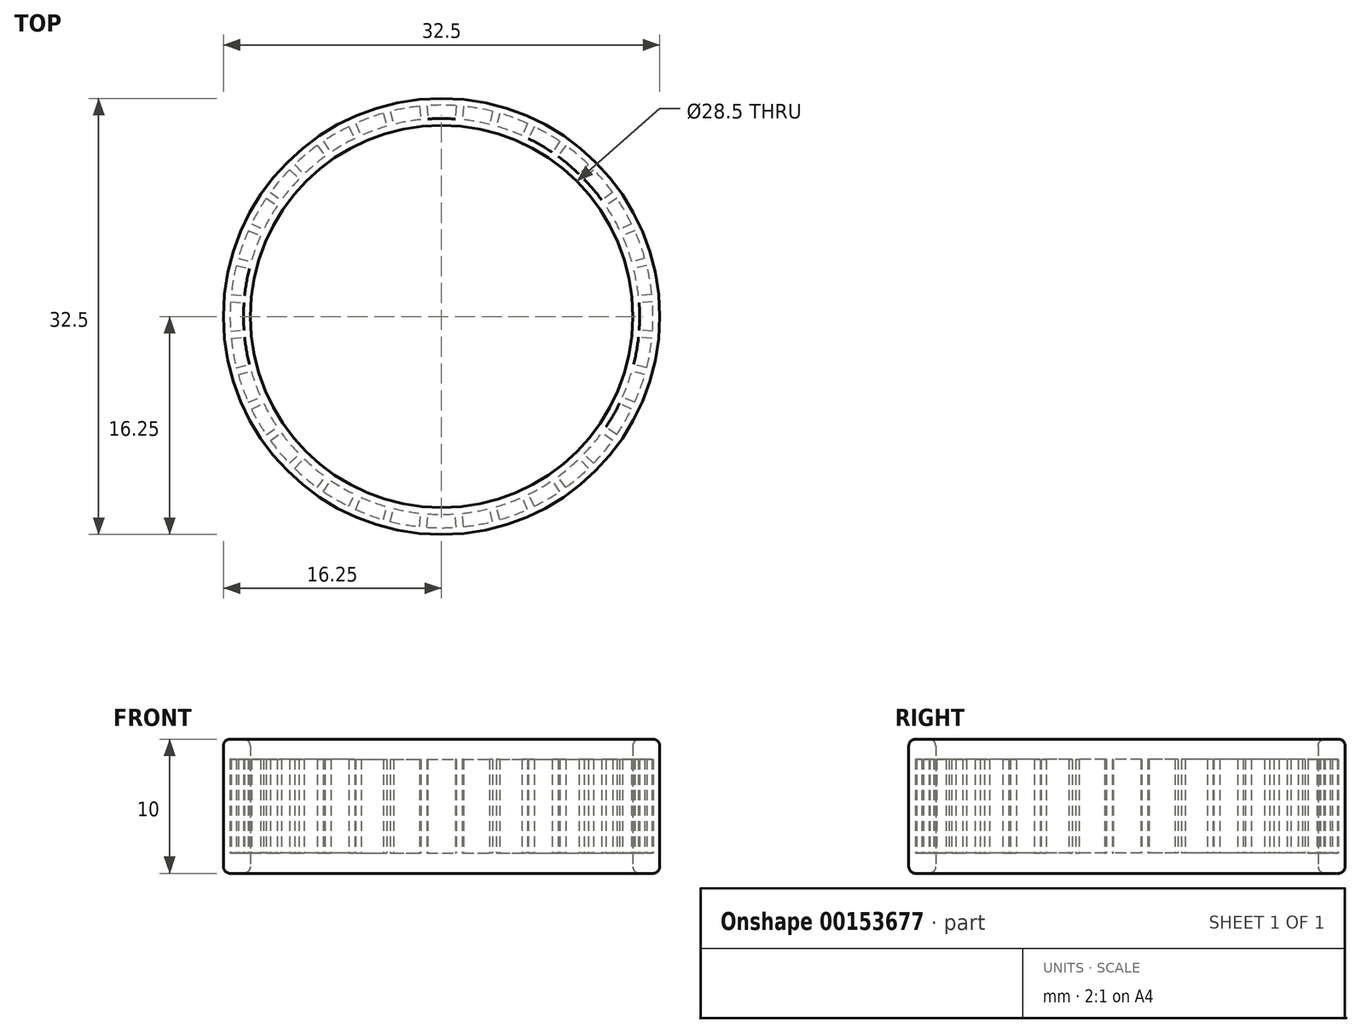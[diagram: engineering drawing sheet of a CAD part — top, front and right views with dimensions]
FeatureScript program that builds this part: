
annotation { "Feature Type Name" : "Feature", "Feature Type Description" : "" }
export const myFeature = defineFeature(function(context is Context, id is Id, definition is map)
    precondition{}
    {
        {
            var Q0;
            Q0=qCreatedBy(makeId("Top.planeOp"),FACE);
            var sketch = newSketch(context, id + "F0", { "sketchPlane" : qUnion([Q0])});
            skCircle(sketch, "E0", {"center": v(0, 0) * mm, "radius": 16.25 * mm});
            skCircle(sketch, "E1", {"center": v(0, 0) * mm, "radius": 14.25 * mm});
            skSolve(sketch);
        }
        {
            var Q0;
            Q0 = qSketchRegion(id + "F0", true);
            var Q1;
            Q1 = qConstructionFilter(qBodyType(qCreatedBy(id + "F0" ,EDGE), BodyType.WIRE), ConstructionObject.NO);
            extrude(context, id + "F1", {"entities" : qUnion([Q0]), "surfaceEntities" : qUnion([Q1]), "depth" : 1.5 * mm});
        }
        {
            var Q0;
            Q0=makeQuery(id+"F1.opExtrude","CAP_FACE",FACE,{"disambiguationData":[OSD([sQuery(id+"F0.wireOp",EDGE,"E0"),sQuery(id+"F0.wireOp",EDGE,"E1")])],"isStart":false});
            var sketch = newSketch(context, id + "F2", { "sketchPlane" : qUnion([Q0])});
            skCircle(sketch, "E2", {"center": v(0, 0) * mm, "radius": 16.25 * mm});
            skCircle(sketch, "E3", {"center": v(0, 0) * mm, "radius": 14.25 * mm});
            skArc(sketch, "E4", {"start": v(-1.03, 14.71) * mm, "mid": v(0, 14.75) * mm, "end": v(1.03, 14.71) * mm});
            skArc(sketch, "E5", {"start": v(-1.1, 15.71) * mm, "mid": v(0, 15.75) * mm, "end": v(1.1, 15.71) * mm});
            skLineSegment(sketch, "E6", {"start": v(-1.1, 15.71) * mm, "end": v(-1.03, 14.71) * mm});
            skLineSegment(sketch, "E7", {"start": v(1.1, 15.71) * mm, "end": v(1.03, 14.71) * mm});
            skLineSegment(sketch, "E8", {"start": v(0, 14.75) * mm, "end": v(0, 15.75) * mm, "construction": true});
            skLineSegment(sketch, "E9.1.0", {"start": v(-1.65, 15.66) * mm, "end": v(-1.54, 14.67) * mm});
            skArc(sketch, "E9.1.1", {"start": v(-3.81, 15.28) * mm, "mid": v(-2.73, 15.51) * mm, "end": v(-1.65, 15.66) * mm});
            skArc(sketch, "E9.1.2", {"start": v(-3.57, 14.31) * mm, "mid": v(-2.56, 14.53) * mm, "end": v(-1.54, 14.67) * mm});
            skLineSegment(sketch, "E9.1.3", {"start": v(-3.81, 15.28) * mm, "end": v(-3.57, 14.31) * mm});
            skLineSegment(sketch, "E9.2.0", {"start": v(-4.34, 15.14) * mm, "end": v(-4.07, 14.18) * mm});
            skArc(sketch, "E9.2.1", {"start": v(-6.4, 14.39) * mm, "mid": v(-5.39, 14.8) * mm, "end": v(-4.34, 15.14) * mm});
            skArc(sketch, "E9.2.2", {"start": v(-6, 13.47) * mm, "mid": v(-5.04, 13.86) * mm, "end": v(-4.07, 14.18) * mm});
            skLineSegment(sketch, "E9.2.3", {"start": v(-6.4, 14.39) * mm, "end": v(-6, 13.47) * mm});
            skLineSegment(sketch, "E9.3.0", {"start": v(-6.9, 14.16) * mm, "end": v(-6.47, 13.26) * mm});
            skArc(sketch, "E9.3.1", {"start": v(-8.8, 13.06) * mm, "mid": v(-7.87, 13.64) * mm, "end": v(-6.9, 14.16) * mm});
            skArc(sketch, "E9.3.2", {"start": v(-8.25, 12.23) * mm, "mid": v(-7.38, 12.77) * mm, "end": v(-6.47, 13.26) * mm});
            skLineSegment(sketch, "E9.3.3", {"start": v(-8.8, 13.06) * mm, "end": v(-8.25, 12.23) * mm});
            skLineSegment(sketch, "E9.4.0", {"start": v(-9.26, 12.74) * mm, "end": v(-8.67, 11.93) * mm});
            skArc(sketch, "E9.4.1", {"start": v(-10.94, 11.33) * mm, "mid": v(-10.12, 12.07) * mm, "end": v(-9.26, 12.74) * mm});
            skArc(sketch, "E9.4.2", {"start": v(-10.25, 10.61) * mm, "mid": v(-9.48, 11.3) * mm, "end": v(-8.67, 11.93) * mm});
            skLineSegment(sketch, "E9.4.3", {"start": v(-10.94, 11.33) * mm, "end": v(-10.25, 10.61) * mm});
            skLineSegment(sketch, "E9.5.0", {"start": v(-11.33, 10.94) * mm, "end": v(-10.61, 10.25) * mm});
            skArc(sketch, "E9.5.1", {"start": v(-12.74, 9.26) * mm, "mid": v(-12.07, 10.12) * mm, "end": v(-11.33, 10.94) * mm});
            skArc(sketch, "E9.5.2", {"start": v(-11.93, 8.67) * mm, "mid": v(-11.3, 9.48) * mm, "end": v(-10.61, 10.25) * mm});
            skLineSegment(sketch, "E9.5.3", {"start": v(-12.74, 9.26) * mm, "end": v(-11.93, 8.67) * mm});
            skLineSegment(sketch, "E9.6.0", {"start": v(-13.06, 8.8) * mm, "end": v(-12.23, 8.25) * mm});
            skArc(sketch, "E9.6.1", {"start": v(-14.16, 6.9) * mm, "mid": v(-13.64, 7.88) * mm, "end": v(-13.06, 8.8) * mm});
            skArc(sketch, "E9.6.2", {"start": v(-13.26, 6.47) * mm, "mid": v(-12.77, 7.38) * mm, "end": v(-12.23, 8.25) * mm});
            skLineSegment(sketch, "E9.6.3", {"start": v(-14.16, 6.9) * mm, "end": v(-13.26, 6.47) * mm});
            skLineSegment(sketch, "E9.7.0", {"start": v(-14.39, 6.4) * mm, "end": v(-13.47, 6) * mm});
            skArc(sketch, "E9.7.1", {"start": v(-15.14, 4.34) * mm, "mid": v(-14.8, 5.39) * mm, "end": v(-14.39, 6.4) * mm});
            skArc(sketch, "E9.7.2", {"start": v(-14.18, 4.07) * mm, "mid": v(-13.86, 5.04) * mm, "end": v(-13.47, 6) * mm});
            skLineSegment(sketch, "E9.7.3", {"start": v(-15.14, 4.34) * mm, "end": v(-14.18, 4.07) * mm});
            skLineSegment(sketch, "E9.8.0", {"start": v(-15.28, 3.81) * mm, "end": v(-14.31, 3.57) * mm});
            skArc(sketch, "E9.8.1", {"start": v(-15.66, 1.65) * mm, "mid": v(-15.51, 2.73) * mm, "end": v(-15.28, 3.81) * mm});
            skArc(sketch, "E9.8.2", {"start": v(-14.67, 1.54) * mm, "mid": v(-14.53, 2.56) * mm, "end": v(-14.31, 3.57) * mm});
            skLineSegment(sketch, "E9.8.3", {"start": v(-15.66, 1.65) * mm, "end": v(-14.67, 1.54) * mm});
            skLineSegment(sketch, "E9.9.0", {"start": v(-15.71, 1.1) * mm, "end": v(-14.71, 1.03) * mm});
            skArc(sketch, "E9.9.1", {"start": v(-15.71, -1.1) * mm, "mid": v(-15.75, 0) * mm, "end": v(-15.71, 1.1) * mm});
            skArc(sketch, "E9.9.2", {"start": v(-14.71, -1.03) * mm, "mid": v(-14.75, 0) * mm, "end": v(-14.71, 1.03) * mm});
            skLineSegment(sketch, "E9.9.3", {"start": v(-15.71, -1.1) * mm, "end": v(-14.71, -1.03) * mm});
            skLineSegment(sketch, "E9.10.0", {"start": v(-15.66, -1.65) * mm, "end": v(-14.67, -1.54) * mm});
            skArc(sketch, "E9.10.1", {"start": v(-15.28, -3.81) * mm, "mid": v(-15.51, -2.73) * mm, "end": v(-15.66, -1.65) * mm});
            skArc(sketch, "E9.10.2", {"start": v(-14.31, -3.57) * mm, "mid": v(-14.53, -2.56) * mm, "end": v(-14.67, -1.54) * mm});
            skLineSegment(sketch, "E9.10.3", {"start": v(-15.28, -3.81) * mm, "end": v(-14.31, -3.57) * mm});
            skLineSegment(sketch, "E9.11.0", {"start": v(-15.14, -4.34) * mm, "end": v(-14.18, -4.07) * mm});
            skArc(sketch, "E9.11.1", {"start": v(-14.39, -6.4) * mm, "mid": v(-14.8, -5.39) * mm, "end": v(-15.14, -4.34) * mm});
            skArc(sketch, "E9.11.2", {"start": v(-13.47, -6) * mm, "mid": v(-13.86, -5.04) * mm, "end": v(-14.18, -4.07) * mm});
            skLineSegment(sketch, "E9.11.3", {"start": v(-14.39, -6.4) * mm, "end": v(-13.47, -6) * mm});
            skLineSegment(sketch, "E9.12.0", {"start": v(-14.16, -6.9) * mm, "end": v(-13.26, -6.47) * mm});
            skArc(sketch, "E9.12.1", {"start": v(-13.06, -8.8) * mm, "mid": v(-13.64, -7.87) * mm, "end": v(-14.16, -6.9) * mm});
            skArc(sketch, "E9.12.2", {"start": v(-12.23, -8.25) * mm, "mid": v(-12.77, -7.37) * mm, "end": v(-13.26, -6.47) * mm});
            skLineSegment(sketch, "E9.12.3", {"start": v(-13.06, -8.8) * mm, "end": v(-12.23, -8.25) * mm});
            skLineSegment(sketch, "E9.13.0", {"start": v(-12.74, -9.26) * mm, "end": v(-11.93, -8.67) * mm});
            skArc(sketch, "E9.13.1", {"start": v(-11.33, -10.94) * mm, "mid": v(-12.07, -10.12) * mm, "end": v(-12.74, -9.26) * mm});
            skArc(sketch, "E9.13.2", {"start": v(-10.61, -10.25) * mm, "mid": v(-11.3, -9.48) * mm, "end": v(-11.93, -8.67) * mm});
            skLineSegment(sketch, "E9.13.3", {"start": v(-11.33, -10.94) * mm, "end": v(-10.61, -10.25) * mm});
            skLineSegment(sketch, "E9.14.0", {"start": v(-10.94, -11.33) * mm, "end": v(-10.25, -10.61) * mm});
            skArc(sketch, "E9.14.1", {"start": v(-9.26, -12.74) * mm, "mid": v(-10.12, -12.07) * mm, "end": v(-10.94, -11.33) * mm});
            skArc(sketch, "E9.14.2", {"start": v(-8.67, -11.93) * mm, "mid": v(-9.48, -11.3) * mm, "end": v(-10.25, -10.61) * mm});
            skLineSegment(sketch, "E9.14.3", {"start": v(-9.26, -12.74) * mm, "end": v(-8.67, -11.93) * mm});
            skLineSegment(sketch, "E9.15.0", {"start": v(-8.8, -13.06) * mm, "end": v(-8.25, -12.23) * mm});
            skArc(sketch, "E9.15.1", {"start": v(-6.9, -14.16) * mm, "mid": v(-7.87, -13.64) * mm, "end": v(-8.8, -13.06) * mm});
            skArc(sketch, "E9.15.2", {"start": v(-6.47, -13.26) * mm, "mid": v(-7.37, -12.77) * mm, "end": v(-8.25, -12.23) * mm});
            skLineSegment(sketch, "E9.15.3", {"start": v(-6.9, -14.16) * mm, "end": v(-6.47, -13.26) * mm});
            skLineSegment(sketch, "E9.16.0", {"start": v(-6.4, -14.39) * mm, "end": v(-6, -13.47) * mm});
            skArc(sketch, "E9.16.1", {"start": v(-4.34, -15.14) * mm, "mid": v(-5.39, -14.8) * mm, "end": v(-6.4, -14.39) * mm});
            skArc(sketch, "E9.16.2", {"start": v(-4.07, -14.18) * mm, "mid": v(-5.04, -13.86) * mm, "end": v(-6, -13.47) * mm});
            skLineSegment(sketch, "E9.16.3", {"start": v(-4.34, -15.14) * mm, "end": v(-4.07, -14.18) * mm});
            skLineSegment(sketch, "E9.17.0", {"start": v(-3.81, -15.28) * mm, "end": v(-3.57, -14.31) * mm});
            skArc(sketch, "E9.17.1", {"start": v(-1.65, -15.66) * mm, "mid": v(-2.73, -15.51) * mm, "end": v(-3.81, -15.28) * mm});
            skArc(sketch, "E9.17.2", {"start": v(-1.54, -14.67) * mm, "mid": v(-2.56, -14.53) * mm, "end": v(-3.57, -14.31) * mm});
            skLineSegment(sketch, "E9.17.3", {"start": v(-1.65, -15.66) * mm, "end": v(-1.54, -14.67) * mm});
            skLineSegment(sketch, "E9.18.0", {"start": v(-1.1, -15.71) * mm, "end": v(-1.03, -14.71) * mm});
            skArc(sketch, "E9.18.1", {"start": v(1.1, -15.71) * mm, "mid": v(0, -15.75) * mm, "end": v(-1.1, -15.71) * mm});
            skArc(sketch, "E9.18.2", {"start": v(1.03, -14.71) * mm, "mid": v(0, -14.75) * mm, "end": v(-1.03, -14.71) * mm});
            skLineSegment(sketch, "E9.18.3", {"start": v(1.1, -15.71) * mm, "end": v(1.03, -14.71) * mm});
            skLineSegment(sketch, "E9.19.0", {"start": v(1.65, -15.66) * mm, "end": v(1.54, -14.67) * mm});
            skArc(sketch, "E9.19.1", {"start": v(3.81, -15.28) * mm, "mid": v(2.73, -15.51) * mm, "end": v(1.65, -15.66) * mm});
            skArc(sketch, "E9.19.2", {"start": v(3.57, -14.31) * mm, "mid": v(2.56, -14.53) * mm, "end": v(1.54, -14.67) * mm});
            skLineSegment(sketch, "E9.19.3", {"start": v(3.81, -15.28) * mm, "end": v(3.57, -14.31) * mm});
            skLineSegment(sketch, "E9.20.0", {"start": v(4.34, -15.14) * mm, "end": v(4.07, -14.18) * mm});
            skArc(sketch, "E9.20.1", {"start": v(6.4, -14.39) * mm, "mid": v(5.39, -14.8) * mm, "end": v(4.34, -15.14) * mm});
            skArc(sketch, "E9.20.2", {"start": v(6, -13.47) * mm, "mid": v(5.04, -13.86) * mm, "end": v(4.07, -14.18) * mm});
            skLineSegment(sketch, "E9.20.3", {"start": v(6.4, -14.39) * mm, "end": v(6, -13.47) * mm});
            skLineSegment(sketch, "E9.21.0", {"start": v(6.9, -14.16) * mm, "end": v(6.47, -13.26) * mm});
            skArc(sketch, "E9.21.1", {"start": v(8.8, -13.06) * mm, "mid": v(7.87, -13.64) * mm, "end": v(6.9, -14.16) * mm});
            skArc(sketch, "E9.21.2", {"start": v(8.25, -12.23) * mm, "mid": v(7.37, -12.77) * mm, "end": v(6.47, -13.26) * mm});
            skLineSegment(sketch, "E9.21.3", {"start": v(8.8, -13.06) * mm, "end": v(8.25, -12.23) * mm});
            skLineSegment(sketch, "E9.22.0", {"start": v(9.26, -12.74) * mm, "end": v(8.67, -11.93) * mm});
            skArc(sketch, "E9.22.1", {"start": v(10.94, -11.33) * mm, "mid": v(10.12, -12.07) * mm, "end": v(9.26, -12.74) * mm});
            skArc(sketch, "E9.22.2", {"start": v(10.25, -10.61) * mm, "mid": v(9.48, -11.3) * mm, "end": v(8.67, -11.93) * mm});
            skLineSegment(sketch, "E9.22.3", {"start": v(10.94, -11.33) * mm, "end": v(10.25, -10.61) * mm});
            skLineSegment(sketch, "E9.23.0", {"start": v(11.33, -10.94) * mm, "end": v(10.61, -10.25) * mm});
            skArc(sketch, "E9.23.1", {"start": v(12.74, -9.26) * mm, "mid": v(12.07, -10.12) * mm, "end": v(11.33, -10.94) * mm});
            skArc(sketch, "E9.23.2", {"start": v(11.93, -8.67) * mm, "mid": v(11.3, -9.48) * mm, "end": v(10.61, -10.25) * mm});
            skLineSegment(sketch, "E9.23.3", {"start": v(12.74, -9.26) * mm, "end": v(11.93, -8.67) * mm});
            skLineSegment(sketch, "E9.24.0", {"start": v(13.06, -8.8) * mm, "end": v(12.23, -8.25) * mm});
            skArc(sketch, "E9.24.1", {"start": v(14.16, -6.9) * mm, "mid": v(13.64, -7.88) * mm, "end": v(13.06, -8.8) * mm});
            skArc(sketch, "E9.24.2", {"start": v(13.26, -6.47) * mm, "mid": v(12.77, -7.38) * mm, "end": v(12.23, -8.25) * mm});
            skLineSegment(sketch, "E9.24.3", {"start": v(14.16, -6.9) * mm, "end": v(13.26, -6.47) * mm});
            skLineSegment(sketch, "E9.25.0", {"start": v(14.39, -6.4) * mm, "end": v(13.47, -6) * mm});
            skArc(sketch, "E9.25.1", {"start": v(15.14, -4.34) * mm, "mid": v(14.8, -5.39) * mm, "end": v(14.39, -6.4) * mm});
            skArc(sketch, "E9.25.2", {"start": v(14.18, -4.07) * mm, "mid": v(13.86, -5.04) * mm, "end": v(13.47, -6) * mm});
            skLineSegment(sketch, "E9.25.3", {"start": v(15.14, -4.34) * mm, "end": v(14.18, -4.07) * mm});
            skLineSegment(sketch, "E9.26.0", {"start": v(15.28, -3.81) * mm, "end": v(14.31, -3.57) * mm});
            skArc(sketch, "E9.26.1", {"start": v(15.66, -1.65) * mm, "mid": v(15.51, -2.73) * mm, "end": v(15.28, -3.81) * mm});
            skArc(sketch, "E9.26.2", {"start": v(14.67, -1.54) * mm, "mid": v(14.53, -2.56) * mm, "end": v(14.31, -3.57) * mm});
            skLineSegment(sketch, "E9.26.3", {"start": v(15.66, -1.65) * mm, "end": v(14.67, -1.54) * mm});
            skLineSegment(sketch, "E9.27.0", {"start": v(15.71, -1.1) * mm, "end": v(14.71, -1.03) * mm});
            skArc(sketch, "E9.27.1", {"start": v(15.71, 1.1) * mm, "mid": v(15.75, 0) * mm, "end": v(15.71, -1.1) * mm});
            skArc(sketch, "E9.27.2", {"start": v(14.71, 1.03) * mm, "mid": v(14.75, 0) * mm, "end": v(14.71, -1.03) * mm});
            skLineSegment(sketch, "E9.27.3", {"start": v(15.71, 1.1) * mm, "end": v(14.71, 1.03) * mm});
            skLineSegment(sketch, "E9.28.0", {"start": v(15.66, 1.65) * mm, "end": v(14.67, 1.54) * mm});
            skArc(sketch, "E9.28.1", {"start": v(15.28, 3.81) * mm, "mid": v(15.51, 2.73) * mm, "end": v(15.66, 1.65) * mm});
            skArc(sketch, "E9.28.2", {"start": v(14.31, 3.57) * mm, "mid": v(14.53, 2.56) * mm, "end": v(14.67, 1.54) * mm});
            skLineSegment(sketch, "E9.28.3", {"start": v(15.28, 3.81) * mm, "end": v(14.31, 3.57) * mm});
            skLineSegment(sketch, "E9.29.0", {"start": v(15.14, 4.34) * mm, "end": v(14.18, 4.07) * mm});
            skArc(sketch, "E9.29.1", {"start": v(14.39, 6.4) * mm, "mid": v(14.8, 5.39) * mm, "end": v(15.14, 4.34) * mm});
            skArc(sketch, "E9.29.2", {"start": v(13.47, 6) * mm, "mid": v(13.86, 5.04) * mm, "end": v(14.18, 4.07) * mm});
            skLineSegment(sketch, "E9.29.3", {"start": v(14.39, 6.4) * mm, "end": v(13.47, 6) * mm});
            skLineSegment(sketch, "E9.30.0", {"start": v(14.16, 6.9) * mm, "end": v(13.26, 6.47) * mm});
            skArc(sketch, "E9.30.1", {"start": v(13.06, 8.8) * mm, "mid": v(13.64, 7.88) * mm, "end": v(14.16, 6.9) * mm});
            skArc(sketch, "E9.30.2", {"start": v(12.23, 8.25) * mm, "mid": v(12.77, 7.38) * mm, "end": v(13.26, 6.47) * mm});
            skLineSegment(sketch, "E9.30.3", {"start": v(13.06, 8.8) * mm, "end": v(12.23, 8.25) * mm});
            skLineSegment(sketch, "E9.31.0", {"start": v(12.74, 9.26) * mm, "end": v(11.93, 8.67) * mm});
            skArc(sketch, "E9.31.1", {"start": v(11.33, 10.94) * mm, "mid": v(12.07, 10.12) * mm, "end": v(12.74, 9.26) * mm});
            skArc(sketch, "E9.31.2", {"start": v(10.61, 10.25) * mm, "mid": v(11.3, 9.48) * mm, "end": v(11.93, 8.67) * mm});
            skLineSegment(sketch, "E9.31.3", {"start": v(11.33, 10.94) * mm, "end": v(10.61, 10.25) * mm});
            skLineSegment(sketch, "E9.32.0", {"start": v(10.94, 11.33) * mm, "end": v(10.25, 10.61) * mm});
            skArc(sketch, "E9.32.1", {"start": v(9.26, 12.74) * mm, "mid": v(10.12, 12.07) * mm, "end": v(10.94, 11.33) * mm});
            skArc(sketch, "E9.32.2", {"start": v(8.67, 11.93) * mm, "mid": v(9.48, 11.3) * mm, "end": v(10.25, 10.61) * mm});
            skLineSegment(sketch, "E9.32.3", {"start": v(9.26, 12.74) * mm, "end": v(8.67, 11.93) * mm});
            skLineSegment(sketch, "E9.33.0", {"start": v(8.8, 13.06) * mm, "end": v(8.25, 12.23) * mm});
            skArc(sketch, "E9.33.1", {"start": v(6.9, 14.16) * mm, "mid": v(7.88, 13.64) * mm, "end": v(8.8, 13.06) * mm});
            skArc(sketch, "E9.33.2", {"start": v(6.47, 13.26) * mm, "mid": v(7.38, 12.77) * mm, "end": v(8.25, 12.23) * mm});
            skLineSegment(sketch, "E9.33.3", {"start": v(6.9, 14.16) * mm, "end": v(6.47, 13.26) * mm});
            skLineSegment(sketch, "E9.34.0", {"start": v(6.4, 14.39) * mm, "end": v(6, 13.47) * mm});
            skArc(sketch, "E9.34.1", {"start": v(4.34, 15.14) * mm, "mid": v(5.39, 14.8) * mm, "end": v(6.4, 14.39) * mm});
            skArc(sketch, "E9.34.2", {"start": v(4.07, 14.18) * mm, "mid": v(5.04, 13.86) * mm, "end": v(6, 13.47) * mm});
            skLineSegment(sketch, "E9.34.3", {"start": v(4.34, 15.14) * mm, "end": v(4.07, 14.18) * mm});
            skLineSegment(sketch, "E9.35.0", {"start": v(3.81, 15.28) * mm, "end": v(3.57, 14.31) * mm});
            skArc(sketch, "E9.35.1", {"start": v(1.65, 15.66) * mm, "mid": v(2.73, 15.51) * mm, "end": v(3.81, 15.28) * mm});
            skArc(sketch, "E9.35.2", {"start": v(1.54, 14.67) * mm, "mid": v(2.56, 14.53) * mm, "end": v(3.57, 14.31) * mm});
            skLineSegment(sketch, "E9.35.3", {"start": v(1.65, 15.66) * mm, "end": v(1.54, 14.67) * mm});
            skSolve(sketch);
        }
        {
            var Q0;
            Q0 = qSketchRegion(id + "F2", true);
            extrude(context, id + "F3", {"entities" : qUnion([Q0]), "operationType" : NewBodyOperationType.ADD, "depth" : 7 * mm});
        }
        {
            var Q0;
            Q0=makeQuery(id+"F3.opExtrude","CAP_FACE",FACE,{"disambiguationData":[OSD([sQuery(id+"F2.wireOp",EDGE,"E2"),sQuery(id+"F2.wireOp",EDGE,"E3"),sQuery(id+"F2.wireOp",EDGE,"E4"),sQuery(id+"F2.wireOp",EDGE,"E5"),sQuery(id+"F2.wireOp",EDGE,"E6"),sQuery(id+"F2.wireOp",EDGE,"E7"),sQuery(id+"F2.wireOp",EDGE,"E9.1.0"),sQuery(id+"F2.wireOp",EDGE,"E9.1.1"),sQuery(id+"F2.wireOp",EDGE,"E9.1.2"),sQuery(id+"F2.wireOp",EDGE,"E9.1.3"),sQuery(id+"F2.wireOp",EDGE,"E9.2.0"),sQuery(id+"F2.wireOp",EDGE,"E9.2.1"),sQuery(id+"F2.wireOp",EDGE,"E9.2.2"),sQuery(id+"F2.wireOp",EDGE,"E9.2.3"),sQuery(id+"F2.wireOp",EDGE,"E9.3.0"),sQuery(id+"F2.wireOp",EDGE,"E9.3.1"),sQuery(id+"F2.wireOp",EDGE,"E9.3.2"),sQuery(id+"F2.wireOp",EDGE,"E9.3.3"),sQuery(id+"F2.wireOp",EDGE,"E9.4.0"),sQuery(id+"F2.wireOp",EDGE,"E9.4.1"),sQuery(id+"F2.wireOp",EDGE,"E9.4.2"),sQuery(id+"F2.wireOp",EDGE,"E9.4.3"),sQuery(id+"F2.wireOp",EDGE,"E9.5.0"),sQuery(id+"F2.wireOp",EDGE,"E9.5.1"),sQuery(id+"F2.wireOp",EDGE,"E9.5.2"),sQuery(id+"F2.wireOp",EDGE,"E9.5.3"),sQuery(id+"F2.wireOp",EDGE,"E9.6.0"),sQuery(id+"F2.wireOp",EDGE,"E9.6.1"),sQuery(id+"F2.wireOp",EDGE,"E9.6.2"),sQuery(id+"F2.wireOp",EDGE,"E9.6.3"),sQuery(id+"F2.wireOp",EDGE,"E9.7.0"),sQuery(id+"F2.wireOp",EDGE,"E9.7.1"),sQuery(id+"F2.wireOp",EDGE,"E9.7.2"),sQuery(id+"F2.wireOp",EDGE,"E9.7.3"),sQuery(id+"F2.wireOp",EDGE,"E9.8.0"),sQuery(id+"F2.wireOp",EDGE,"E9.8.1"),sQuery(id+"F2.wireOp",EDGE,"E9.8.2"),sQuery(id+"F2.wireOp",EDGE,"E9.8.3"),sQuery(id+"F2.wireOp",EDGE,"E9.9.0"),sQuery(id+"F2.wireOp",EDGE,"E9.9.1"),sQuery(id+"F2.wireOp",EDGE,"E9.9.2"),sQuery(id+"F2.wireOp",EDGE,"E9.9.3"),sQuery(id+"F2.wireOp",EDGE,"E9.10.0"),sQuery(id+"F2.wireOp",EDGE,"E9.10.1"),sQuery(id+"F2.wireOp",EDGE,"E9.10.2"),sQuery(id+"F2.wireOp",EDGE,"E9.10.3"),sQuery(id+"F2.wireOp",EDGE,"E9.11.0"),sQuery(id+"F2.wireOp",EDGE,"E9.11.1"),sQuery(id+"F2.wireOp",EDGE,"E9.11.2"),sQuery(id+"F2.wireOp",EDGE,"E9.11.3"),sQuery(id+"F2.wireOp",EDGE,"E9.12.0"),sQuery(id+"F2.wireOp",EDGE,"E9.12.1"),sQuery(id+"F2.wireOp",EDGE,"E9.12.2"),sQuery(id+"F2.wireOp",EDGE,"E9.12.3"),sQuery(id+"F2.wireOp",EDGE,"E9.13.0"),sQuery(id+"F2.wireOp",EDGE,"E9.13.1"),sQuery(id+"F2.wireOp",EDGE,"E9.13.2"),sQuery(id+"F2.wireOp",EDGE,"E9.13.3"),sQuery(id+"F2.wireOp",EDGE,"E9.14.0"),sQuery(id+"F2.wireOp",EDGE,"E9.14.1"),sQuery(id+"F2.wireOp",EDGE,"E9.14.2"),sQuery(id+"F2.wireOp",EDGE,"E9.14.3"),sQuery(id+"F2.wireOp",EDGE,"E9.15.0"),sQuery(id+"F2.wireOp",EDGE,"E9.15.1"),sQuery(id+"F2.wireOp",EDGE,"E9.15.2"),sQuery(id+"F2.wireOp",EDGE,"E9.15.3"),sQuery(id+"F2.wireOp",EDGE,"E9.16.0"),sQuery(id+"F2.wireOp",EDGE,"E9.16.1"),sQuery(id+"F2.wireOp",EDGE,"E9.16.2"),sQuery(id+"F2.wireOp",EDGE,"E9.16.3"),sQuery(id+"F2.wireOp",EDGE,"E9.17.0"),sQuery(id+"F2.wireOp",EDGE,"E9.17.1"),sQuery(id+"F2.wireOp",EDGE,"E9.17.2"),sQuery(id+"F2.wireOp",EDGE,"E9.17.3"),sQuery(id+"F2.wireOp",EDGE,"E9.18.0"),sQuery(id+"F2.wireOp",EDGE,"E9.18.1"),sQuery(id+"F2.wireOp",EDGE,"E9.18.2"),sQuery(id+"F2.wireOp",EDGE,"E9.18.3"),sQuery(id+"F2.wireOp",EDGE,"E9.19.0"),sQuery(id+"F2.wireOp",EDGE,"E9.19.1"),sQuery(id+"F2.wireOp",EDGE,"E9.19.2"),sQuery(id+"F2.wireOp",EDGE,"E9.19.3"),sQuery(id+"F2.wireOp",EDGE,"E9.20.0"),sQuery(id+"F2.wireOp",EDGE,"E9.20.1"),sQuery(id+"F2.wireOp",EDGE,"E9.20.2"),sQuery(id+"F2.wireOp",EDGE,"E9.20.3"),sQuery(id+"F2.wireOp",EDGE,"E9.21.0"),sQuery(id+"F2.wireOp",EDGE,"E9.21.1"),sQuery(id+"F2.wireOp",EDGE,"E9.21.2"),sQuery(id+"F2.wireOp",EDGE,"E9.21.3"),sQuery(id+"F2.wireOp",EDGE,"E9.22.0"),sQuery(id+"F2.wireOp",EDGE,"E9.22.1"),sQuery(id+"F2.wireOp",EDGE,"E9.22.2"),sQuery(id+"F2.wireOp",EDGE,"E9.22.3"),sQuery(id+"F2.wireOp",EDGE,"E9.23.0"),sQuery(id+"F2.wireOp",EDGE,"E9.23.1"),sQuery(id+"F2.wireOp",EDGE,"E9.23.2"),sQuery(id+"F2.wireOp",EDGE,"E9.23.3"),sQuery(id+"F2.wireOp",EDGE,"E9.24.0"),sQuery(id+"F2.wireOp",EDGE,"E9.24.1"),sQuery(id+"F2.wireOp",EDGE,"E9.24.2"),sQuery(id+"F2.wireOp",EDGE,"E9.24.3"),sQuery(id+"F2.wireOp",EDGE,"E9.25.0"),sQuery(id+"F2.wireOp",EDGE,"E9.25.1"),sQuery(id+"F2.wireOp",EDGE,"E9.25.2"),sQuery(id+"F2.wireOp",EDGE,"E9.25.3"),sQuery(id+"F2.wireOp",EDGE,"E9.26.0"),sQuery(id+"F2.wireOp",EDGE,"E9.26.1"),sQuery(id+"F2.wireOp",EDGE,"E9.26.2"),sQuery(id+"F2.wireOp",EDGE,"E9.26.3"),sQuery(id+"F2.wireOp",EDGE,"E9.27.0"),sQuery(id+"F2.wireOp",EDGE,"E9.27.1"),sQuery(id+"F2.wireOp",EDGE,"E9.27.2"),sQuery(id+"F2.wireOp",EDGE,"E9.27.3"),sQuery(id+"F2.wireOp",EDGE,"E9.28.0"),sQuery(id+"F2.wireOp",EDGE,"E9.28.1"),sQuery(id+"F2.wireOp",EDGE,"E9.28.2"),sQuery(id+"F2.wireOp",EDGE,"E9.28.3"),sQuery(id+"F2.wireOp",EDGE,"E9.29.0"),sQuery(id+"F2.wireOp",EDGE,"E9.29.1"),sQuery(id+"F2.wireOp",EDGE,"E9.29.2"),sQuery(id+"F2.wireOp",EDGE,"E9.29.3"),sQuery(id+"F2.wireOp",EDGE,"E9.30.0"),sQuery(id+"F2.wireOp",EDGE,"E9.30.1"),sQuery(id+"F2.wireOp",EDGE,"E9.30.2"),sQuery(id+"F2.wireOp",EDGE,"E9.30.3"),sQuery(id+"F2.wireOp",EDGE,"E9.31.0"),sQuery(id+"F2.wireOp",EDGE,"E9.31.1"),sQuery(id+"F2.wireOp",EDGE,"E9.31.2"),sQuery(id+"F2.wireOp",EDGE,"E9.31.3"),sQuery(id+"F2.wireOp",EDGE,"E9.32.0"),sQuery(id+"F2.wireOp",EDGE,"E9.32.1"),sQuery(id+"F2.wireOp",EDGE,"E9.32.2"),sQuery(id+"F2.wireOp",EDGE,"E9.32.3"),sQuery(id+"F2.wireOp",EDGE,"E9.33.0"),sQuery(id+"F2.wireOp",EDGE,"E9.33.1"),sQuery(id+"F2.wireOp",EDGE,"E9.33.2"),sQuery(id+"F2.wireOp",EDGE,"E9.33.3"),sQuery(id+"F2.wireOp",EDGE,"E9.34.0"),sQuery(id+"F2.wireOp",EDGE,"E9.34.1"),sQuery(id+"F2.wireOp",EDGE,"E9.34.2"),sQuery(id+"F2.wireOp",EDGE,"E9.34.3"),sQuery(id+"F2.wireOp",EDGE,"E9.35.0"),sQuery(id+"F2.wireOp",EDGE,"E9.35.1"),sQuery(id+"F2.wireOp",EDGE,"E9.35.2"),sQuery(id+"F2.wireOp",EDGE,"E9.35.3")])],"isStart":false});
            var sketch = newSketch(context, id + "F4", { "sketchPlane" : qUnion([Q0])});
            skCircle(sketch, "E10", {"center": v(0, 0) * mm, "radius": 16.25 * mm});
            skCircle(sketch, "E11", {"center": v(0, 0) * mm, "radius": 14.25 * mm});
            skSolve(sketch);
        }
        {
            var Q0;
            Q0 = qSketchRegion(id + "F4", true);
            extrude(context, id + "F5", {"entities" : qUnion([Q0]), "operationType" : NewBodyOperationType.ADD, "depth" : 1.5 * mm});
        }
        {
            var Q0;
            Q0=makeQuery(id+"F5.opExtrude","CAP_EDGE",EDGE,{"disambiguationData":[OSD([sQuery(id+"F4.wireOp",EDGE,"E10")])],"isStart":false});
            var Q1;
            Q1=makeQuery(id+"F5.opExtrude","CAP_EDGE",EDGE,{"disambiguationData":[OSD([sQuery(id+"F4.wireOp",EDGE,"E11")])],"isStart":false});
            var Q2;
            Q2=makeQuery(id+"F1.opExtrude","CAP_EDGE",EDGE,{"disambiguationData":[OSD([sQuery(id+"F0.wireOp",EDGE,"E1")])],"isStart":true});
            var Q3;
            Q3=makeQuery(id+"F1.opExtrude","CAP_EDGE",EDGE,{"disambiguationData":[OSD([sQuery(id+"F0.wireOp",EDGE,"E0")])],"isStart":true});
            fillet(context, id + "F6", {"entities" : qUnion([Q0, Q1, Q2, Q3]), "radius" : 0.5 * mm, "tangentPropagation" : true, "allowEdgeOverflow" : false});
        }
    });
